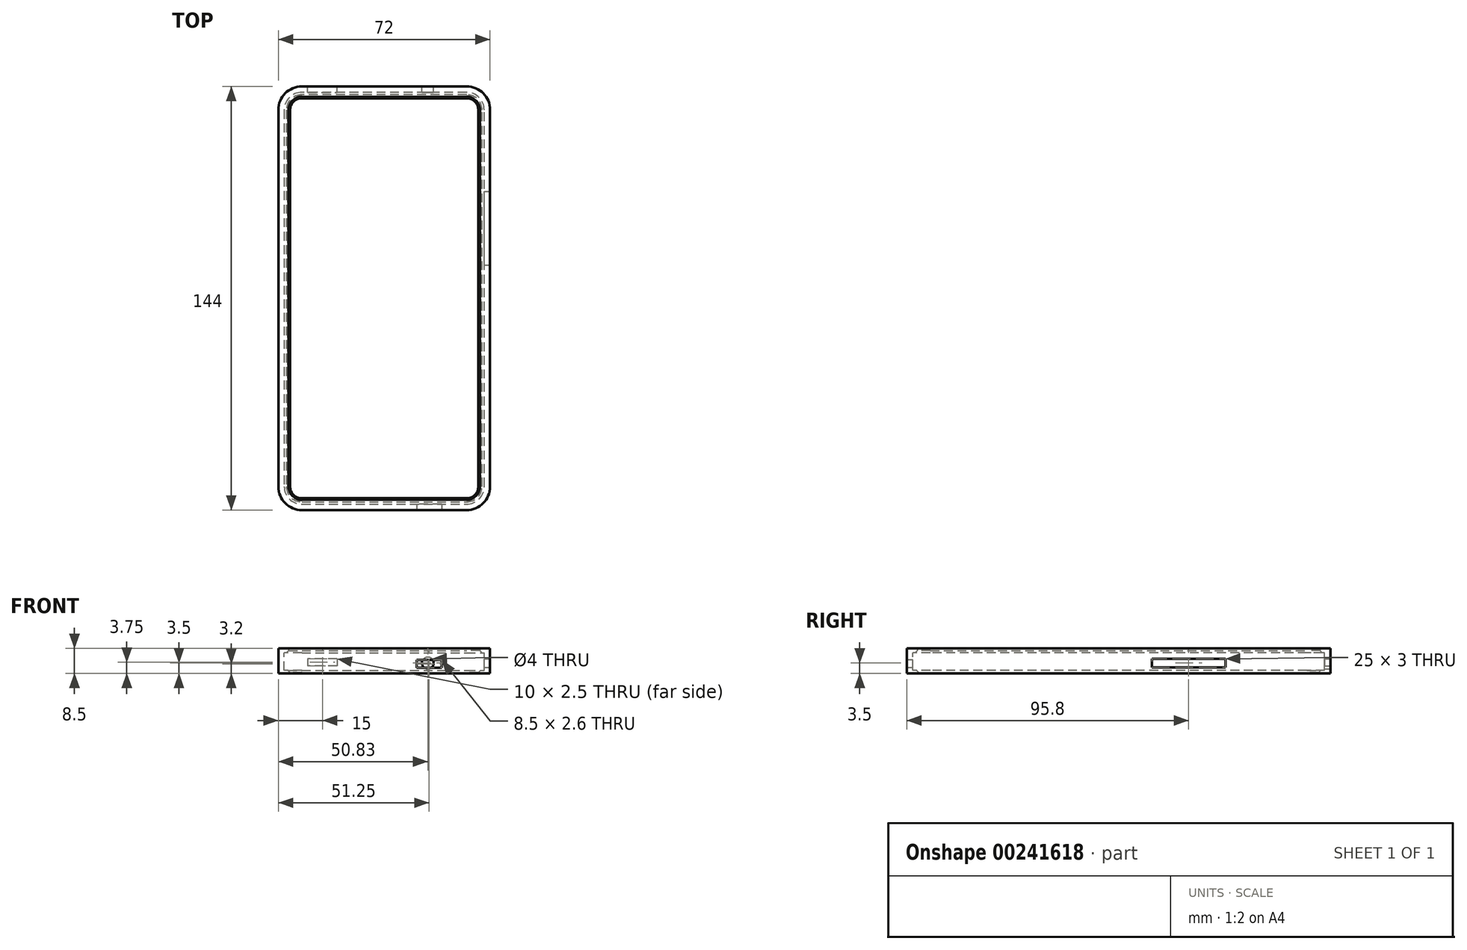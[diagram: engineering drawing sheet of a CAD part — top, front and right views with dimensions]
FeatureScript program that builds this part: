
annotation { "Feature Type Name" : "Feature", "Feature Type Description" : "" }
export const myFeature = defineFeature(function(context is Context, id is Id, definition is map)
    precondition{}
    {
        {
            var Q0;
            Q0=qCreatedBy(makeId("Top.planeOp"),FACE);
            var sketch = newSketch(context, id + "F0", { "sketchPlane" : qUnion([Q0])});
            skLineSegment(sketch, "E0.bottom", {"start": v(-36, 72) * mm, "end": v(36, 72) * mm});
            skLineSegment(sketch, "E0.top", {"start": v(-36, -72) * mm, "end": v(36, -72) * mm});
            skLineSegment(sketch, "E0.left", {"start": v(-36, 72) * mm, "end": v(-36, -72) * mm});
            skLineSegment(sketch, "E0.right", {"start": v(36, 72) * mm, "end": v(36, -72) * mm});
            skLineSegment(sketch, "E1", {"start": v(0, 55.37) * mm, "end": v(0, -119.8) * mm, "construction": true});
            skLineSegment(sketch, "E2", {"start": v(50.74, 0) * mm, "end": v(-70.74, 0) * mm, "construction": true});
            skSolve(sketch);
        }
        {
            var Q0;
            Q0=makeQuery(id+"F0.imprint","IMPRINT",FACE,{"disambiguationData":[TD([[makeQuery(id+"F0.imprint","IMPRINT",EDGE,{"derivedFrom":sQuery(id+"F0.wireOp",EDGE,"E0.bottom")}),-1.0]])]});
            extrude(context, id + "F1", {"entities" : qUnion([Q0]), "depth" : 6 * mm});
        }
        {
            var Q0;
            Q0=makeQuery(id+"F1.opExtrude","SWEPT_EDGE",EDGE,{"disambiguationData":[OSD([sQuery(id+"F0.wireOp",EDGE,"E0.bottom"),sQuery(id+"F0.wireOp",EDGE,"E0.left")])]});
            var Q1;
            Q1=makeQuery(id+"F1.opExtrude","SWEPT_EDGE",EDGE,{"disambiguationData":[OSD([sQuery(id+"F0.wireOp",EDGE,"E0.bottom"),sQuery(id+"F0.wireOp",EDGE,"E0.right")])]});
            var Q2;
            Q2=makeQuery(id+"F1.opExtrude","SWEPT_EDGE",EDGE,{"disambiguationData":[OSD([sQuery(id+"F0.wireOp",EDGE,"E0.top"),sQuery(id+"F0.wireOp",EDGE,"E0.right")])]});
            var Q3;
            Q3=makeQuery(id+"F1.opExtrude","SWEPT_EDGE",EDGE,{"disambiguationData":[OSD([sQuery(id+"F0.wireOp",EDGE,"E0.top"),sQuery(id+"F0.wireOp",EDGE,"E0.left")])]});
            fillet(context, id + "F2", {"entities" : qUnion([Q0, Q1, Q2, Q3]), "radius" : 8 * mm, "tangentPropagation" : true, "allowEdgeOverflow" : false});
        }
        {
            var Q0;
            Q0=qCreatedBy(makeId("Top.planeOp"),FACE);
            var sketch = newSketch(context, id + "F3", { "sketchPlane" : qUnion([Q0])});
            skCircle(sketch, "E3", {"center": v(0, 47) * mm, "radius": 5.8 * mm});
            skCircle(sketch, "E4", {"center": v(9.6, 47) * mm, "radius": 2 * mm});
            skLineSegment(sketch, "E5.0", {"start": v(-28, 72) * mm, "end": v(28, 72) * mm, "construction": true});
            skSolve(sketch);
        }
        {
            var Q0;
            Q0 = qSketchRegion(id + "F3", true);
            extrude(context, id + "F4", {"entities" : qUnion([Q0]), "operationType" : NewBodyOperationType.REMOVE, "oppositeDirection" : true, "depth" : 25 * mm});
        }
        {
            var Q0;
            Q0=makeQuery(id+"F1.opExtrude","SWEPT_FACE",FACE,{"disambiguationData":[OSD([sQuery(id+"F0.wireOp",EDGE,"E0.right")])]});
            var sketch = newSketch(context, id + "F5", { "sketchPlane" : qUnion([Q0])});
            skLineSegment(sketch, "E6.bottom", {"start": v(36.3, 4) * mm, "end": v(11.3, 4) * mm});
            skLineSegment(sketch, "E6.top", {"start": v(36.3, 1) * mm, "end": v(11.3, 1) * mm});
            skLineSegment(sketch, "E6.left", {"start": v(36.3, 4) * mm, "end": v(36.3, 1) * mm});
            skLineSegment(sketch, "E6.right", {"start": v(11.3, 4) * mm, "end": v(11.3, 1) * mm});
            skLineSegment(sketch, "E7.0", {"start": v(72, 6) * mm, "end": v(72, -1.54) * mm, "construction": true});
            skSolve(sketch);
        }
        {
            var Q0;
            Q0 = qSketchRegion(id + "F5", true);
            extrude(context, id + "F6", {"entities" : qUnion([Q0]), "operationType" : NewBodyOperationType.REMOVE, "oppositeDirection" : true, "depth" : 25 * mm});
        }
        {
            var Q0;
            Q0=makeQuery(id+"FDgRIaQ6P2poOzs_1.boolean.opBoolean","MERGE",FACE,{"derivedFrom":[makeQuery(id+"F1.opExtrude","SWEPT_FACE",FACE,{"disambiguationData":[OSD([sQuery(id+"F0.wireOp",EDGE,"E0.top")])]}),makeQuery(id+"FDgRIaQ6P2poOzs_1.opExtrude","CAP_FACE",FACE,{"disambiguationData":[OSD([sQuery(id+"FMSKLPqt1qxX155_1.wireOp",EDGE,"Vr9o5jU8-ENa0-NXIi-TrE8-tDNUzPF5lXwY"),sQuery(id+"FMSKLPqt1qxX155_1.wireOp",EDGE,"itpPHdvN-X94m-TedV-sO2I-Zd1y5aE4VLI5")])],"isStart":false})]});
            var sketch = newSketch(context, id + "F7", { "sketchPlane" : qUnion([Q0])});
            skLineSegment(sketch, "E8.bottom", {"start": v(11, 3.5) * mm, "end": v(19.5, 3.5) * mm});
            skLineSegment(sketch, "E8.top", {"start": v(11, 0.9) * mm, "end": v(19.5, 0.9) * mm});
            skLineSegment(sketch, "E8.left", {"start": v(11, 3.5) * mm, "end": v(11, 0.9) * mm});
            skLineSegment(sketch, "E8.right", {"start": v(19.5, 3.5) * mm, "end": v(19.5, 0.9) * mm});
            skCircle(sketch, "E9", {"center": v(25.85, 4.5) * mm, "radius": 0.35 * mm});
            skSolve(sketch);
        }
        {
            var Q0;
            Q0=makeQuery(id+"F7.imprint","IMPRINT",FACE,{"disambiguationData":[TD([[makeQuery(id+"F7.imprint","IMPRINT",EDGE,{"derivedFrom":sQuery(id+"F7.wireOp",EDGE,"E8.bottom")}),-1.0]])]});
            extrude(context, id + "F8", {"entities" : qUnion([Q0]), "operationType" : NewBodyOperationType.REMOVE, "oppositeDirection" : true, "depth" : 25 * mm});
        }
        {
            var Q0;
            Q0=makeQuery(id+"FDgRIaQ6P2poOzs_1.boolean.opBoolean","MERGE",FACE,{"derivedFrom":[makeQuery(id+"F1.opExtrude","SWEPT_FACE",FACE,{"disambiguationData":[OSD([sQuery(id+"F0.wireOp",EDGE,"E0.bottom")])]}),makeQuery(id+"FDgRIaQ6P2poOzs_1.opExtrude","CAP_FACE",FACE,{"disambiguationData":[OSD([sQuery(id+"FMSKLPqt1qxX155_1.wireOp",EDGE,"Vr9o5jU8-ENa0-NXIi-TrE8-tDNUzPF5lXwY"),sQuery(id+"FMSKLPqt1qxX155_1.wireOp",EDGE,"itpPHdvN-X94m-TedV-sO2I-Zd1y5aE4VLI5")])],"isStart":true})]});
            var sketch = newSketch(context, id + "F9", { "sketchPlane" : qUnion([Q0])});
            skCircle(sketch, "E10", {"center": v(-14.83, 2.5) * mm, "radius": 2 * mm});
            skLineSegment(sketch, "E11.bottom", {"start": v(16, 4) * mm, "end": v(26, 4) * mm});
            skLineSegment(sketch, "E11.top", {"start": v(16, 1.5) * mm, "end": v(26, 1.5) * mm});
            skLineSegment(sketch, "E11.left", {"start": v(16, 4) * mm, "end": v(16, 1.5) * mm});
            skLineSegment(sketch, "E11.right", {"start": v(26, 4) * mm, "end": v(26, 1.5) * mm});
            skLineSegment(sketch, "E12.0", {"start": v(36, 6) * mm, "end": v(36, 0) * mm, "construction": true});
            skLineSegment(sketch, "E13.0", {"start": v(-36, 0) * mm, "end": v(-36, 6) * mm, "construction": true});
            skLineSegment(sketch, "E14.0", {"start": v(28, 6) * mm, "end": v(-28, 6) * mm, "construction": true});
            skSolve(sketch);
        }
        {
            var Q0;
            Q0 = qSketchRegion(id + "F9", true);
            extrude(context, id + "F10", {"entities" : qUnion([Q0]), "operationType" : NewBodyOperationType.REMOVE, "oppositeDirection" : true, "depth" : 25 * mm});
        }
        {
            var Q0;
            Q0=makeQuery(id+"F1.opExtrude","CAP_FACE",FACE,{"disambiguationData":[OSD([sQuery(id+"F0.wireOp",EDGE,"E0.bottom"),sQuery(id+"F0.wireOp",EDGE,"E0.top"),sQuery(id+"F0.wireOp",EDGE,"E0.left"),sQuery(id+"F0.wireOp",EDGE,"E0.right")])],"isStart":false});
            var sketch = newSketch(context, id + "F11", { "sketchPlane" : qUnion([Q0])});
            skArc(sketch, "E15.0", {"start": v(-28, 70) * mm, "mid": v(-32.24, 68.24) * mm, "end": v(-34, 64) * mm});
            skLineSegment(sketch, "E15.1", {"start": v(28, 70) * mm, "end": v(-28, 70) * mm});
            skLineSegment(sketch, "E15.2", {"start": v(-34, 64) * mm, "end": v(-34, -64) * mm});
            skArc(sketch, "E15.3", {"start": v(34, 64) * mm, "mid": v(32.24, 68.24) * mm, "end": v(28, 70) * mm});
            skArc(sketch, "E15.4", {"start": v(-34, -64) * mm, "mid": v(-32.24, -68.24) * mm, "end": v(-28, -70) * mm});
            skLineSegment(sketch, "E15.5", {"start": v(-28, -70) * mm, "end": v(28, -70) * mm});
            skArc(sketch, "E15.6", {"start": v(28, -70) * mm, "mid": v(32.24, -68.24) * mm, "end": v(34, -64) * mm});
            skLineSegment(sketch, "E15.7", {"start": v(34, -64) * mm, "end": v(34, 64) * mm});
            skSolve(sketch);
        }
        {
            var Q0;
            Q0=makeQuery(id+"F11.imprint","IMPRINT",FACE,{"disambiguationData":[TD([[makeQuery(id+"F11.imprint","IMPRINT",EDGE,{"derivedFrom":sQuery(id+"F11.wireOp",EDGE,"E15.0")}),1.0]])]});
            extrude(context, id + "F12", {"entities" : qUnion([Q0]), "operationType" : NewBodyOperationType.REMOVE, "oppositeDirection" : true, "depth" : 25 * mm});
        }
        {
            var Q0;
            Q0=makeQuery(id+"F1.opExtrude","CAP_FACE",FACE,{"disambiguationData":[OSD([sQuery(id+"F0.wireOp",EDGE,"E0.bottom"),sQuery(id+"F0.wireOp",EDGE,"E0.top"),sQuery(id+"F0.wireOp",EDGE,"E0.left"),sQuery(id+"F0.wireOp",EDGE,"E0.right")])],"isStart":false});
            var sketch = newSketch(context, id + "F13", { "sketchPlane" : qUnion([Q0])});
            skLineSegment(sketch, "E16.0", {"start": v(-28, 72) * mm, "end": v(28, 72) * mm});
            skArc(sketch, "E17.0", {"start": v(-28, 72) * mm, "mid": v(-33.66, 69.66) * mm, "end": v(-36, 64) * mm});
            skLineSegment(sketch, "E18.0", {"start": v(-36, 64) * mm, "end": v(-36, -64) * mm});
            skArc(sketch, "E19.0", {"start": v(36, 64) * mm, "mid": v(33.66, 69.66) * mm, "end": v(28, 72) * mm});
            skLineSegment(sketch, "E20.0", {"start": v(36, 64) * mm, "end": v(36, -64) * mm});
            skArc(sketch, "E21.0", {"start": v(28, -72) * mm, "mid": v(33.66, -69.66) * mm, "end": v(36, -64) * mm});
            skLineSegment(sketch, "E22.0", {"start": v(-28, -72) * mm, "end": v(28, -72) * mm});
            skArc(sketch, "E23.0", {"start": v(-36, -64) * mm, "mid": v(-33.66, -69.66) * mm, "end": v(-28, -72) * mm});
            skArc(sketch, "E24.0", {"start": v(-32.5, -64) * mm, "mid": v(-31.18, -67.18) * mm, "end": v(-28, -68.5) * mm});
            skLineSegment(sketch, "E24.1", {"start": v(-32.5, 64) * mm, "end": v(-32.5, -64) * mm});
            skLineSegment(sketch, "E24.2", {"start": v(-28, -68.5) * mm, "end": v(28, -68.5) * mm});
            skArc(sketch, "E24.3", {"start": v(-28, 68.5) * mm, "mid": v(-31.18, 67.18) * mm, "end": v(-32.5, 64) * mm});
            skArc(sketch, "E24.4", {"start": v(28, -68.5) * mm, "mid": v(31.18, -67.18) * mm, "end": v(32.5, -64) * mm});
            skLineSegment(sketch, "E24.5", {"start": v(32.5, -64) * mm, "end": v(32.5, 64) * mm});
            skArc(sketch, "E24.6", {"start": v(32.5, 64) * mm, "mid": v(31.18, 67.18) * mm, "end": v(28, 68.5) * mm});
            skLineSegment(sketch, "E24.7", {"start": v(28, 68.5) * mm, "end": v(-28, 68.5) * mm});
            skSolve(sketch);
        }
        {
            var Q0;
            Q0 = qSketchRegion(id + "F13", true);
            extrude(context, id + "F14", {"entities" : qUnion([Q0]), "operationType" : NewBodyOperationType.ADD, "depth" : 1.5 * mm});
        }
        {
            var Q0;
            Q0=makeQuery(id+"F1.opExtrude","CAP_FACE",FACE,{"disambiguationData":[OSD([sQuery(id+"F0.wireOp",EDGE,"E0.bottom"),sQuery(id+"F0.wireOp",EDGE,"E0.top"),sQuery(id+"F0.wireOp",EDGE,"E0.left"),sQuery(id+"F0.wireOp",EDGE,"E0.right")])],"isStart":true});
            var sketch = newSketch(context, id + "F15", { "sketchPlane" : qUnion([Q0])});
            skArc(sketch, "E25.0", {"start": v(28, -72) * mm, "mid": v(33.66, -69.66) * mm, "end": v(36, -64) * mm});
            skLineSegment(sketch, "E26.0", {"start": v(-28, -72) * mm, "end": v(28, -72) * mm});
            skArc(sketch, "E27.0", {"start": v(-36, -64) * mm, "mid": v(-33.66, -69.66) * mm, "end": v(-28, -72) * mm});
            skLineSegment(sketch, "E28.0", {"start": v(-36, -64) * mm, "end": v(-36, 64) * mm});
            skLineSegment(sketch, "E29.0", {"start": v(36, -64) * mm, "end": v(36, 64) * mm});
            skArc(sketch, "E30.0", {"start": v(36, 64) * mm, "mid": v(33.66, 69.66) * mm, "end": v(28, 72) * mm});
            skLineSegment(sketch, "E31.0", {"start": v(-28, 72) * mm, "end": v(28, 72) * mm});
            skLineSegment(sketch, "E32.0", {"start": v(-28, 68) * mm, "end": v(28, 68) * mm});
            skArc(sketch, "E32.1", {"start": v(-32, 64) * mm, "mid": v(-30.83, 66.83) * mm, "end": v(-28, 68) * mm});
            skArc(sketch, "E32.2", {"start": v(28, 68) * mm, "mid": v(30.83, 66.83) * mm, "end": v(32, 64) * mm});
            skLineSegment(sketch, "E32.3", {"start": v(-32, -64) * mm, "end": v(-32, 64) * mm});
            skLineSegment(sketch, "E32.4", {"start": v(32, 64) * mm, "end": v(32, -64) * mm});
            skArc(sketch, "E32.5", {"start": v(32, -64) * mm, "mid": v(30.83, -66.83) * mm, "end": v(28, -68) * mm});
            skLineSegment(sketch, "E32.6", {"start": v(28, -68) * mm, "end": v(-28, -68) * mm});
            skArc(sketch, "E32.7", {"start": v(-28, -68) * mm, "mid": v(-30.83, -66.83) * mm, "end": v(-32, -64) * mm});
            skSolve(sketch);
        }
        {
            var Q0;
            Q0=makeQuery(id+"F15.imprint","IMPRINT",FACE,{"disambiguationData":[TD([[makeQuery(id+"F15.imprint","IMPRINT",EDGE,{"derivedFrom":sQuery(id+"F15.wireOp",EDGE,"E32.0")}),1.0]])]});
            var Q1;
            Q1=makeQuery(id+"F15.imprint","IMPRINT",FACE,{"disambiguationData":[TD([[makeQuery(id+"F15.imprint","IMPRINT",EDGE,{"derivedFrom":sQuery(id+"F15.wireOp",EDGE,"E25.0")}),1.0]])]});
            extrude(context, id + "F16", {"entities" : qUnion([Q0, Q1]), "operationType" : NewBodyOperationType.ADD, "depth" : 1 * mm});
        }
        {
            var Q0;
            Q0=makeQuery(id+"F16.opExtrude","CAP_EDGE",EDGE,{"disambiguationData":[OSD([sQuery(id+"F15.wireOp",EDGE,"E32.2")])],"isStart":true});
            var Q1;
            Q1=makeQuery(id+"F14.opExtrude","CAP_EDGE",EDGE,{"disambiguationData":[OSD([sQuery(id+"F13.wireOp",EDGE,"E24.4")])],"isStart":true});
            chamfer(context, id + "F17", {"entities" : qUnion([Q0, Q1]), "width" : .75 * mm, "tangentPropagation" : true});
        }
    });
